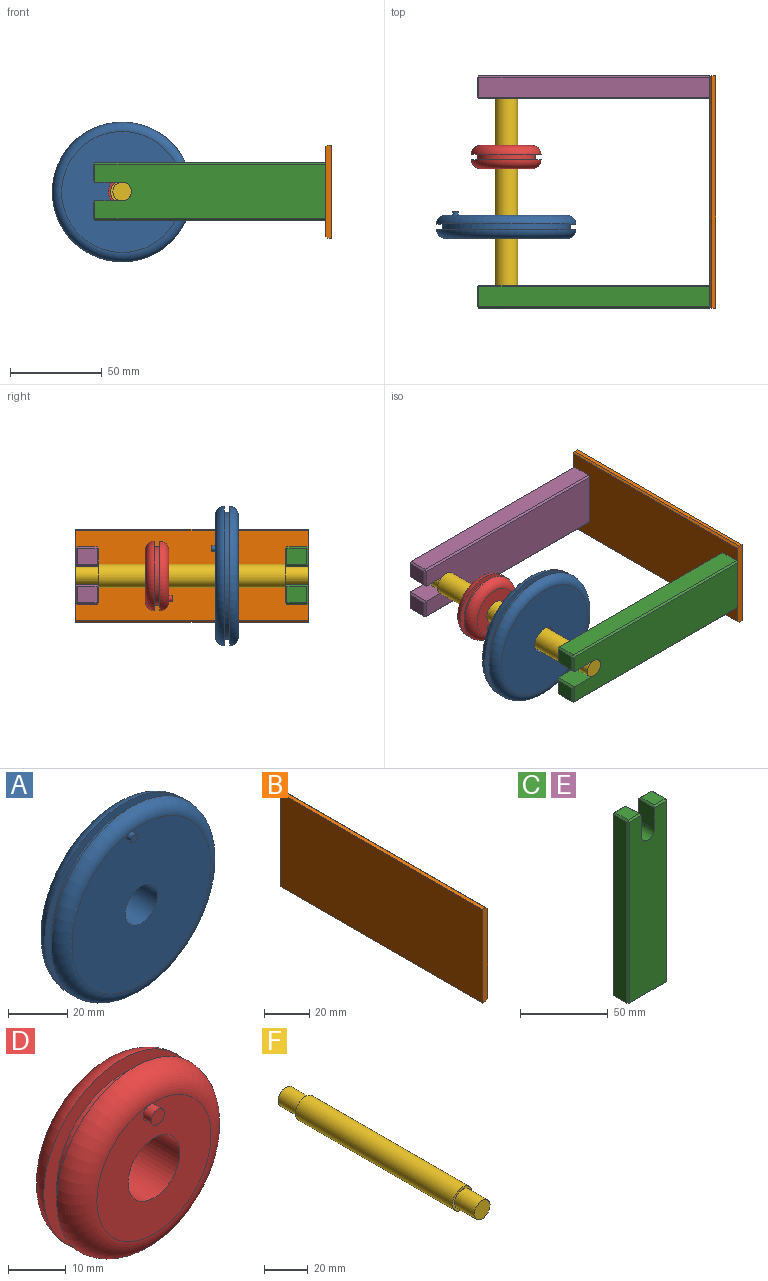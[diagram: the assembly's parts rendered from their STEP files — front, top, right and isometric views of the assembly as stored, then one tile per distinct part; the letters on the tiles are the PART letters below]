
ASSEMBLY  parts=6 mates=5
PART A: 10 faces, bbox 82.5x14.7x82.5 mm
  f0: cylinder r=7.62mm len=15.24mm, axis (0,1,0), area 608mm2, adj f1,f2
  f1: plane 66.06x66.06mm, normal (0,-1,0), area 3237.1mm2, adj f0,f7,f8
  f2: plane 66.06x66.06mm, normal (0,1,0), area 3245mm2, adj f0,f6
  f3: cylinder r=34.92mm len=69.85mm, axis (0,-1,0), area 696.7mm2, adj f4,f5
  f4: plane 76.2x76.2mm, normal (0,-1,0), area 728.4mm2, adj f3,f6
  f5: plane 76.2x76.2mm, normal (0,1,0), area 728.4mm2, adj f3,f7
  f6: torus R=33.03mm, axis (0,1,0), area 1742.1mm2, adj f2,f4
  f7: torus R=33.03mm, axis (0,1,0), area 1742.1mm2, adj f1,f5
  f8: cylinder r=1.59mm len=3.18mm, axis (0,1,0), area 19.9mm2, adj f1,f9
  f9: plane 3.18x3.18mm, normal (0,-1,0), area 7.9mm2, adj f8
PART B: 8 faces, bbox 3.2x127x50.8 mm
  f0: plane 127x2.18mm, normal (0,0,-1), area 276.2mm2, adj f1,f3,f5,f6
  f1: plane 50.8x3.18mm, normal (0,1,0), area 160.3mm2, adj f0,f2,f4,f5,f6,f7
  f2: plane 127x2.18mm, normal (0,0,1), area 276.2mm2, adj f1,f3,f5,f7
  f3: plane 50.8x3.18mm, normal (0,-1,0), area 160.3mm2, adj f0,f2,f4,f5,f6,f7
  f4: plane 127x48.8mm, normal (1,0,0), area 6197.6mm2, adj f1,f3,f6,f7
  f5: plane 127x50.8mm, normal (-1,0,0), area 6451.6mm2, adj f0,f1,f2,f3
  f6: plane 127x1mm, normal (0.71,0,-0.71), area 179.6mm2, adj f0,f1,f3,f4
  f7: plane 127x1mm, normal (0.71,0,0.71), area 179.6mm2, adj f1,f2,f3,f4
PART C: 26 faces, bbox 31.8x12.7x127 mm
  f0: plane 14.88x12.7mm, normal (1,0,0), area 188.9mm2, adj f7,f8,f9,f25
  f1: plane 10.7x8.8mm, normal (0,0,1), area 94.1mm2, adj f19,f23,f24,f25
  f2: plane 126x10.7mm, normal (-1,0,0), area 1348.2mm2, adj f3,f18,f19,f20
  f3: plane 31.75x12.7mm, normal (0,0,-1), area 401.2mm2, adj f2,f4,f8,f9,f10,f11,f18,f20
  f4: plane 126x10.7mm, normal (1,0,0), area 1348.2mm2, adj f3,f10,f11,f12
  f5: plane 10.7x8.8mm, normal (0,0,1), area 94.1mm2, adj f12,f15,f16,f17
  f6: plane 14.88x12.7mm, normal (-1,0,0), area 188.9mm2, adj f7,f8,f9,f17
  f7: cylinder r=5.08mm len=12.7mm, axis (0,1,0), area 202.7mm2, adj f0,f6,f8,f9
  f8: plane 126x29.75mm, normal (0,-1,0), area 3556.8mm2, adj f0,f3,f6,f7,f10,f15,f18,f23
  f9: plane 126x29.75mm, normal (0,1,0), area 3556.8mm2, adj f0,f3,f6,f7,f11,f16,f20,f24
  f10: plane 126x1mm, normal (0.71,-0.71,0), area 178.2mm2, adj f3,f4,f8,f13
  f11: plane 126x1mm, normal (0.71,0.71,0), area 178.2mm2, adj f3,f4,f9,f14
  f12: plane 10.7x1mm, normal (0.71,0,0.71), area 15.1mm2, adj f4,f5,f13,f14
  f13: plane 1x1mm, normal (0.58,-0.58,0.58), area 0.9mm2, adj f10,f12,f15
  f14: plane 1x1mm, normal (0.58,0.58,0.58), area 0.9mm2, adj f11,f12,f16
  f15: plane 9.8x1mm, normal (0,-0.71,0.71), area 13.1mm2, adj f5,f8,f13,f17
  f16: plane 9.8x1mm, normal (0,0.71,0.71), area 13.1mm2, adj f5,f9,f14,f17
  f17: plane 12.7x1mm, normal (-0.71,0,0.71), area 16.5mm2, adj f5,f6,f15,f16
  f18: plane 126x1mm, normal (-0.71,-0.71,0), area 178.2mm2, adj f2,f3,f8,f21
  f19: plane 10.7x1mm, normal (-0.71,0,0.71), area 15.1mm2, adj f1,f2,f21,f22
  f20: plane 126x1mm, normal (-0.71,0.71,0), area 178.2mm2, adj f2,f3,f9,f22
  f21: plane 1x1mm, normal (-0.58,-0.58,0.58), area 0.9mm2, adj f18,f19,f23
  f22: plane 1x1mm, normal (-0.58,0.58,0.58), area 0.9mm2, adj f19,f20,f24
  f23: plane 9.8x1mm, normal (0,-0.71,0.71), area 13.1mm2, adj f1,f8,f21,f25
  f24: plane 9.8x1mm, normal (0,0.71,0.71), area 13.1mm2, adj f1,f9,f22,f25
  f25: plane 12.7x1mm, normal (0.71,0,0.71), area 16.5mm2, adj f0,f1,f23,f24
PART D: 10 faces, bbox 41.3x14.7x41.3 mm
  f0: cylinder r=6.35mm len=12.7mm, axis (0,-1,0), area 506.7mm2, adj f1,f2
  f1: plane 27.96x27.96mm, normal (0,1,0), area 487.3mm2, adj f0,f7
  f2: plane 27.96x27.96mm, normal (0,-1,0), area 479.4mm2, adj f0,f6,f8
  f3: cylinder r=15.88mm len=31.75mm, axis (0,-1,0), area 316.7mm2, adj f4,f5
  f4: plane 38.1x38.1mm, normal (0,-1,0), area 348.4mm2, adj f3,f7
  f5: plane 38.1x38.1mm, normal (0,1,0), area 348.4mm2, adj f3,f6
  f6: torus R=13.98mm, axis (0,1,0), area 825mm2, adj f2,f5
  f7: torus R=13.98mm, axis (0,1,0), area 825mm2, adj f1,f4
  f8: cylinder r=1.59mm len=3.18mm, axis (0,1,0), area 19.9mm2, adj f2,f9
  f9: plane 3.18x3.18mm, normal (0,-1,0), area 7.9mm2, adj f8
PART E: same geometry as C
PART F: 7 faces, bbox 12.7x127x12.7 mm
  f0: cylinder r=6.35mm len=101.6mm, axis (0,1,0), area 4053.7mm2, adj f1,f2
  f1: plane 12.7x12.7mm, normal (0,-1,0), area 45.6mm2, adj f0,f5
  f2: plane 12.7x12.7mm, normal (0,1,0), area 45.6mm2, adj f0,f4
  f3: plane 10.16x10.16mm, normal (0,1,0), area 81.1mm2, adj f4
  f4: cylinder r=5.08mm len=12.7mm, axis (0,1,0), area 405.4mm2, adj f2,f3
  f5: cylinder r=5.08mm len=12.7mm, axis (0,1,0), area 405.4mm2, adj f1,f6
  f6: plane 10.16x10.16mm, normal (0,-1,0), area 81.1mm2, adj f5
PLACE A rot(axis=(0.58,0,-0.81),180deg) t=(-114.3,-19.05,-0.2)mm
PLACE B rot(axis=(0,1,0),180deg) t=(0,0,0)mm
PLACE C rot(axis=(0,-1,0),90deg) t=(-66.68,-50.8,0)mm
PLACE D rot(axis=(0,-1,0),177.7deg) t=(-114.3,19.05,-0.2)mm
PLACE E rot(axis=(0,-1,0),90deg) t=(-66.68,63.5,0)mm
PLACE F rot(axis=(0,-1,0),90deg) t=(-114.3,0,0)mm
MATE fastened E.f9 <-> B.f1  axis (0,1,0) through (-3.17,63.5,0)mm
MATE revolute A.f0 <-> F.f0  axis (0,1,0) through (-114.3,-12.7,-0.2)mm
MATE revolute F.f0 <-> D.f0  axis (0,1,0) through (-114.3,0,-0.2)mm
MATE fastened B.f3 <-> C.f8  axis (0,-1,0) through (-3.18,-63.5,0)mm
MATE fastened C.f7 <-> F.f4  axis (0,1,0) through (-114.3,-63.5,0)mm
